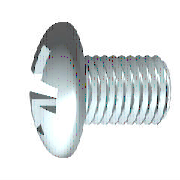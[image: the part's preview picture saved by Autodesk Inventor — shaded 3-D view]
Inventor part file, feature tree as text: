
AUTODESK INVENTOR PART (.ipt)
format: ipt  version: 2018.1 (Build 221171000, 171)  size: 284,672 bytes
history: native  units: mm (DEFAULTED — no unit token found)
features: extrude x1, other x1, plane x1
ambient origin geometry x7: Origin, YZ Plane, XZ Plane, X Axis, Y Axis, Z Axis, Center Point
bodies: Solid1 (feature_tree), Body (feature_tree)
feature tree (3):
  extrude  "Slot"  Depth=2.5mm
  other  "Cut"
  plane  "Work Plane3"
